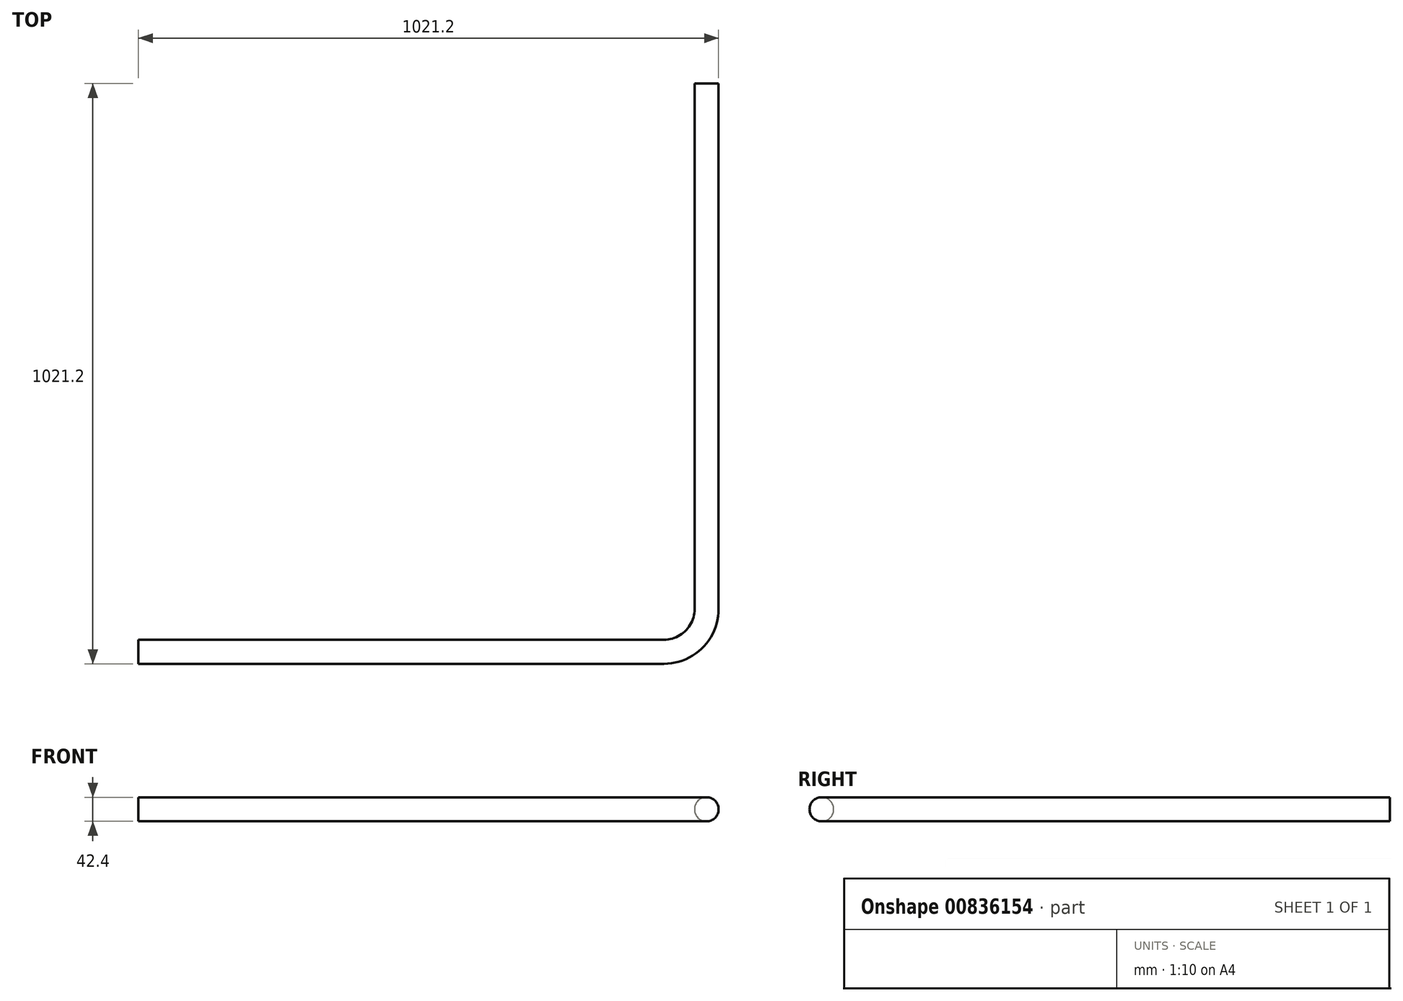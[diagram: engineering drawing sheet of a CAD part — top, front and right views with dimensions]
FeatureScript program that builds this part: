
annotation { "Feature Type Name" : "Feature", "Feature Type Description" : "" }
export const myFeature = defineFeature(function(context is Context, id is Id, definition is map)
    precondition{}
    {
        {
            var Q0;
            Q0=qCreatedBy(makeId("Top.planeOp"),FACE);
            var sketch = newSketch(context, id + "F0", { "sketchPlane" : qUnion([Q0])});
            skLineSegment(sketch, "E0", {"start": v(0, 0) * mm, "end": v(925, 0) * mm});
            skLineSegment(sketch, "E1", {"start": v(1000, 75) * mm, "end": v(1000, 1000) * mm});
            skPoint(sketch, "E2.visualSharp", {"position": v(1000, 0) * mm});
            skArc(sketch, "E2.filletArc", {"start": v(925, 0) * mm, "mid": v(978.03, 21.97) * mm, "end": v(1000, 75) * mm});
            skSolve(sketch);
        }
        {
            var Q0;
            Q0=qCreatedBy(makeId("Right.planeOp"),FACE);
            var sketch = newSketch(context, id + "F1", { "sketchPlane" : qUnion([Q0])});
            skCircle(sketch, "E3", {"center": v(0, 0) * mm, "radius": 21.2 * mm});
            skSolve(sketch);
        }
        {
            var Q0;
            Q0=makeQuery(id+"F1.imprint","IMPRINT",FACE,{"disambiguationData":[TD([[makeQuery(id+"F1.imprint","IMPRINT",EDGE,{"derivedFrom":sQuery(id+"F1.wireOp",EDGE,"E3")}),1.0]])]});
            var Q1;
            Q1=sQuery(id+"F0.wireOp",EDGE,"E0");
            var Q2;
            Q2=sQuery(id+"F0.wireOp",EDGE,"E2.filletArc");
            var Q3;
            Q3=sQuery(id+"F0.wireOp",EDGE,"E1");
            sweep(context, id + "F2", {"profiles" : qUnion([Q0]), "path" : qUnion([Q1, Q2, Q3])});
        }
    });
